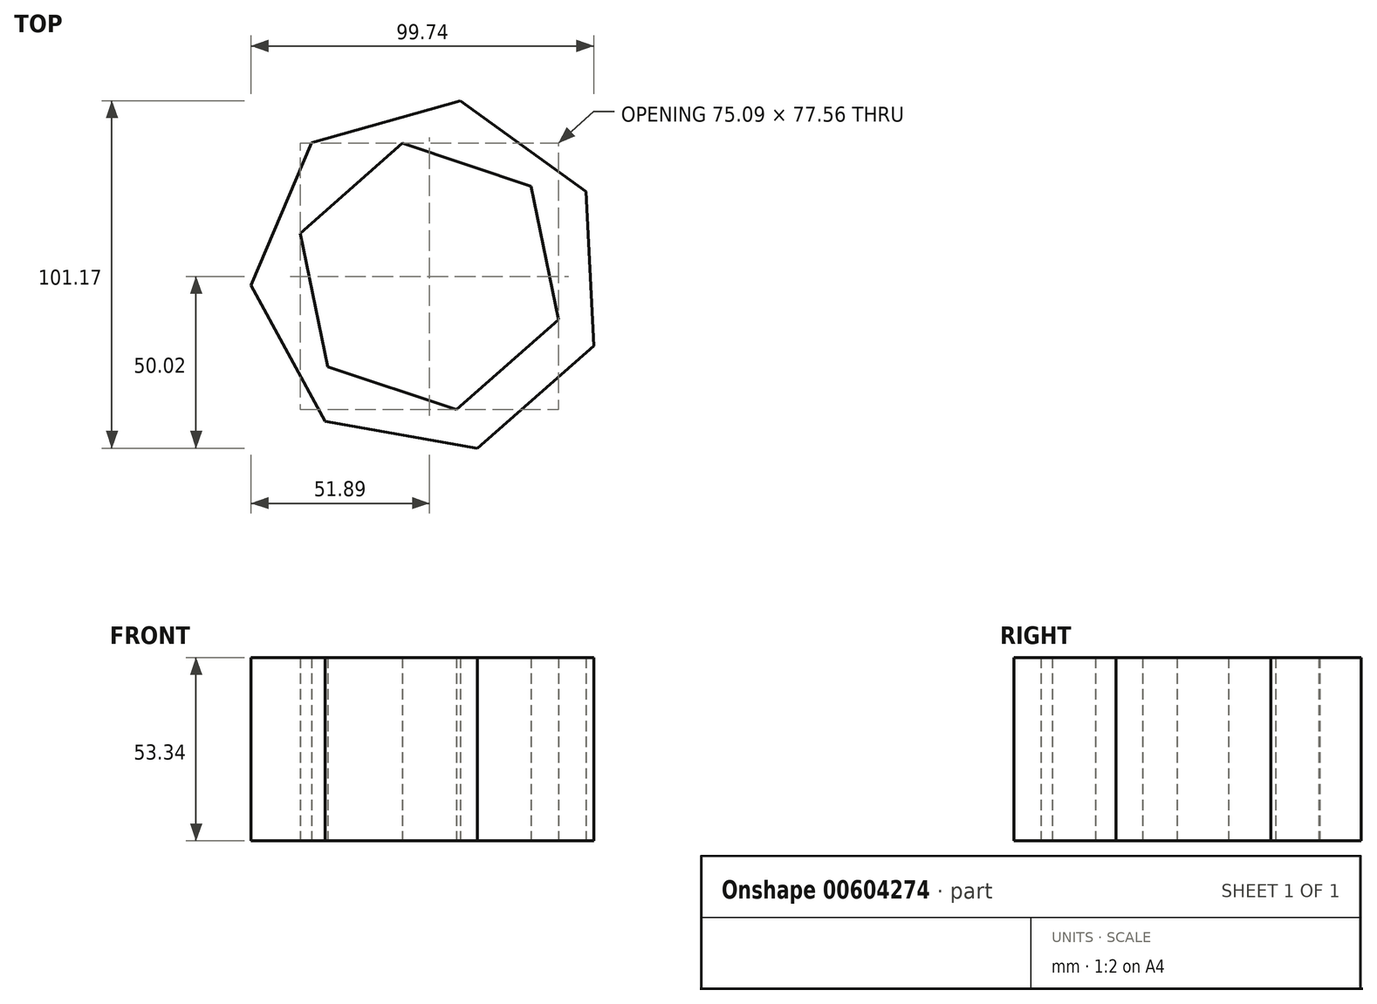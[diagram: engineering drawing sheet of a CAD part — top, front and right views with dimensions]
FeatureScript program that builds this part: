
annotation { "Feature Type Name" : "Feature", "Feature Type Description" : "" }
export const myFeature = defineFeature(function(context is Context, id is Id, definition is map)
    precondition{}
    {
        {
            var Q0;
            Q0=qCreatedBy(makeId("Top.planeOp"),FACE);
            var sketch = newSketch(context, id + "F0", { "sketchPlane" : qUnion([Q0])});
            skCircle(sketch, "E0.cCircle", {"center": v(0, 0) * mm, "radius": 46.8 * mm, "construction": true});
            skLineSegment(sketch, "E0.0", {"start": v(47.85, -20.23) * mm, "end": v(14.02, -50.02) * mm});
            skLineSegment(sketch, "E0.1", {"start": v(14.02, -50.02) * mm, "end": v(-30.37, -42.15) * mm});
            skLineSegment(sketch, "E0.2", {"start": v(-30.37, -42.15) * mm, "end": v(-51.89, -2.53) * mm});
            skLineSegment(sketch, "E0.3", {"start": v(-51.89, -2.53) * mm, "end": v(-34.33, 38.99) * mm});
            skLineSegment(sketch, "E0.4", {"start": v(-34.33, 38.99) * mm, "end": v(9.08, 51.15) * mm});
            skLineSegment(sketch, "E0.5", {"start": v(9.08, 51.15) * mm, "end": v(45.65, 24.8) * mm});
            skLineSegment(sketch, "E0.6", {"start": v(45.65, 24.8) * mm, "end": v(47.85, -20.23) * mm});
            skPoint(sketch, "E0.0.midPoint", {"position": v(30.93, -35.13) * mm});
            skCircle(sketch, "E1.cCircle", {"center": v(0, 0) * mm, "radius": 34.28 * mm, "construction": true});
            skLineSegment(sketch, "E1.0", {"start": v(37.55, -12.53) * mm, "end": v(7.92, -38.78) * mm});
            skLineSegment(sketch, "E1.1", {"start": v(7.92, -38.78) * mm, "end": v(-29.63, -26.25) * mm});
            skLineSegment(sketch, "E1.2", {"start": v(-29.63, -26.25) * mm, "end": v(-37.55, 12.53) * mm});
            skLineSegment(sketch, "E1.3", {"start": v(-37.55, 12.53) * mm, "end": v(-7.92, 38.78) * mm});
            skLineSegment(sketch, "E1.4", {"start": v(-7.92, 38.78) * mm, "end": v(29.63, 26.25) * mm});
            skLineSegment(sketch, "E1.5", {"start": v(29.63, 26.25) * mm, "end": v(37.55, -12.53) * mm});
            skPoint(sketch, "E1.0.midPoint", {"position": v(22.73, -25.66) * mm});
            skSolve(sketch);
        }
        {
            var Q0;
            Q0 = qSketchRegion(id + "F0", true);
            extrude(context, id + "F1", {"entities" : qUnion([Q0]), "depth" : 53.34 * mm, "offsetDistance" : 25.4 * mm});
        }
    });
